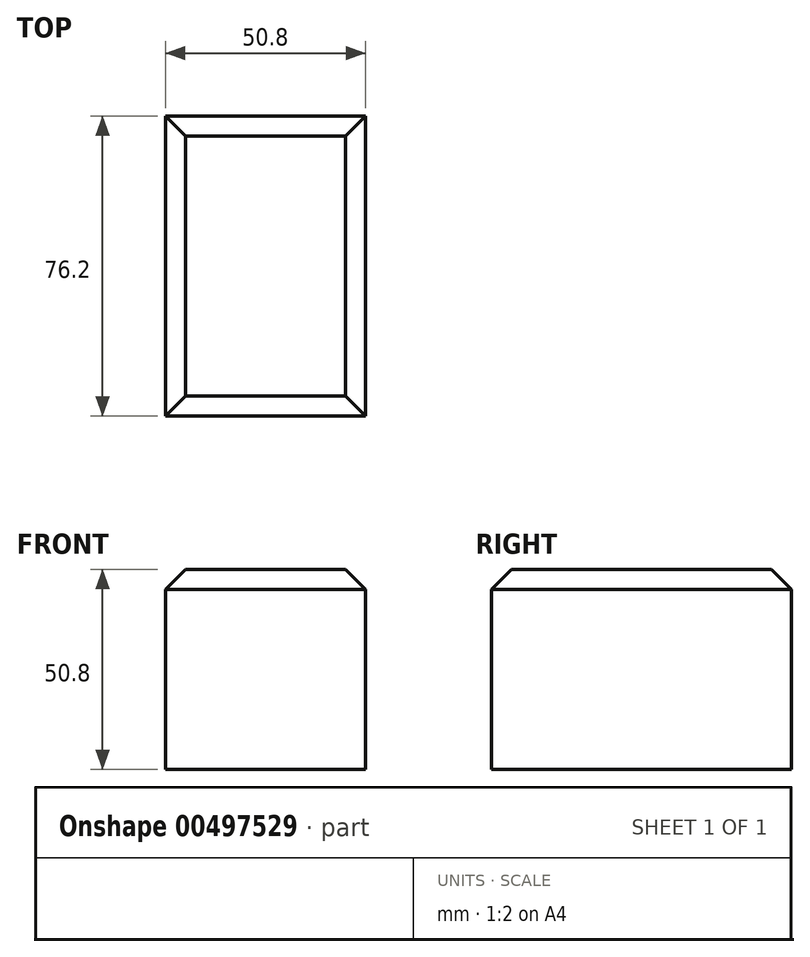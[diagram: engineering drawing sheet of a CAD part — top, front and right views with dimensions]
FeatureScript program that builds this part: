
annotation { "Feature Type Name" : "Feature", "Feature Type Description" : "" }
export const myFeature = defineFeature(function(context is Context, id is Id, definition is map)
    precondition{}
    {
        {
            var Q0;
            Q0=qCreatedBy(makeId("Top.planeOp"),FACE);
            var sketch = newSketch(context, id + "F0", { "sketchPlane" : qUnion([Q0])});
            skLineSegment(sketch, "E0.bottom", {"start": v(-25.9, 40.59) * mm, "end": v(24.9, 40.59) * mm});
            skLineSegment(sketch, "E0.top", {"start": v(-25.9, -35.61) * mm, "end": v(24.9, -35.61) * mm});
            skLineSegment(sketch, "E0.left", {"start": v(-25.9, 40.59) * mm, "end": v(-25.9, -35.61) * mm});
            skLineSegment(sketch, "E0.right", {"start": v(24.9, 40.59) * mm, "end": v(24.9, -35.61) * mm});
            skSolve(sketch);
        }
        {
            var Q0;
            Q0 = qSketchRegion(id + "F0", true);
            extrude(context, id + "F1", {"entities" : qUnion([Q0]), "depth" : 50.8 * mm});
        }
        {
            var Q0;
            Q0=makeQuery(id+"F1.opExtrude","CAP_EDGE",EDGE,{"disambiguationData":[OSD([sQuery(id+"F0.wireOp",EDGE,"E0.top")])],"isStart":false});
            var Q1;
            Q1=makeQuery(id+"F1.opExtrude","CAP_EDGE",EDGE,{"disambiguationData":[OSD([sQuery(id+"F0.wireOp",EDGE,"E0.right")])],"isStart":false});
            var Q2;
            Q2=makeQuery(id+"F1.opExtrude","CAP_EDGE",EDGE,{"disambiguationData":[OSD([sQuery(id+"F0.wireOp",EDGE,"E0.bottom")])],"isStart":false});
            var Q3;
            Q3=makeQuery(id+"F1.opExtrude","CAP_FACE",FACE,{"disambiguationData":[OSD([sQuery(id+"F0.wireOp",EDGE,"E0.bottom"),sQuery(id+"F0.wireOp",EDGE,"E0.top"),sQuery(id+"F0.wireOp",EDGE,"E0.left"),sQuery(id+"F0.wireOp",EDGE,"E0.right")])],"isStart":false});
            chamfer(context, id + "F2", {"entities" : qUnion([Q0, Q1, Q2, Q3]), "width" : 5.08 * mm, "tangentPropagation" : true});
        }
    });
